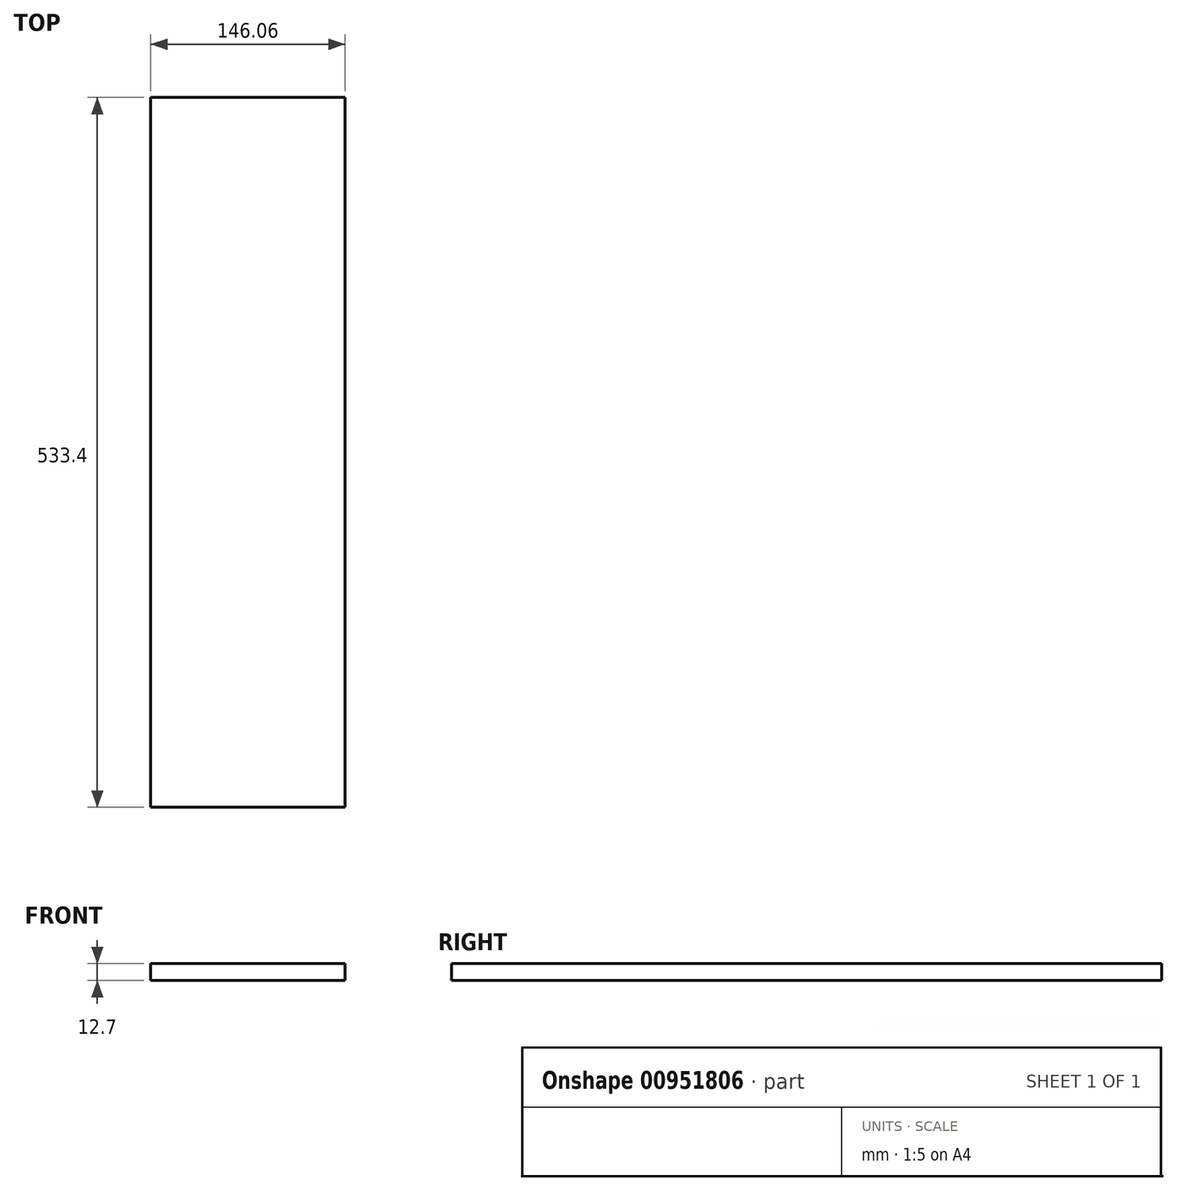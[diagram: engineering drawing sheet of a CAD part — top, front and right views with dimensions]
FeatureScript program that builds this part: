
annotation { "Feature Type Name" : "Feature", "Feature Type Description" : "" }
export const myFeature = defineFeature(function(context is Context, id is Id, definition is map)
    precondition{}
    {
        {
            var Q0;
            Q0=qCreatedBy(makeId("Top.planeOp"),FACE);
            var sketch = newSketch(context, id + "F0", { "sketchPlane" : qUnion([Q0])});
            skLineSegment(sketch, "E0.bottom", {"start": v(73.02, -266.7) * mm, "end": v(-73.03, -266.7) * mm});
            skLineSegment(sketch, "E0.top", {"start": v(73.02, 266.7) * mm, "end": v(-73.03, 266.7) * mm});
            skLineSegment(sketch, "E0.left", {"start": v(73.02, -266.7) * mm, "end": v(73.02, 266.7) * mm});
            skLineSegment(sketch, "E0.right", {"start": v(-73.03, -266.7) * mm, "end": v(-73.03, 266.7) * mm});
            skPoint(sketch, "E0.middle", {"position": v(0, 0) * mm});
            skSolve(sketch);
        }
        {
            var Q0;
            Q0 = qSketchRegion(id + "F0", true);
            extrude(context, id + "F1", {"entities" : qUnion([Q0]), "depth" : 12.7 * mm, "offsetDistance" : 25.4 * mm});
        }
    });
